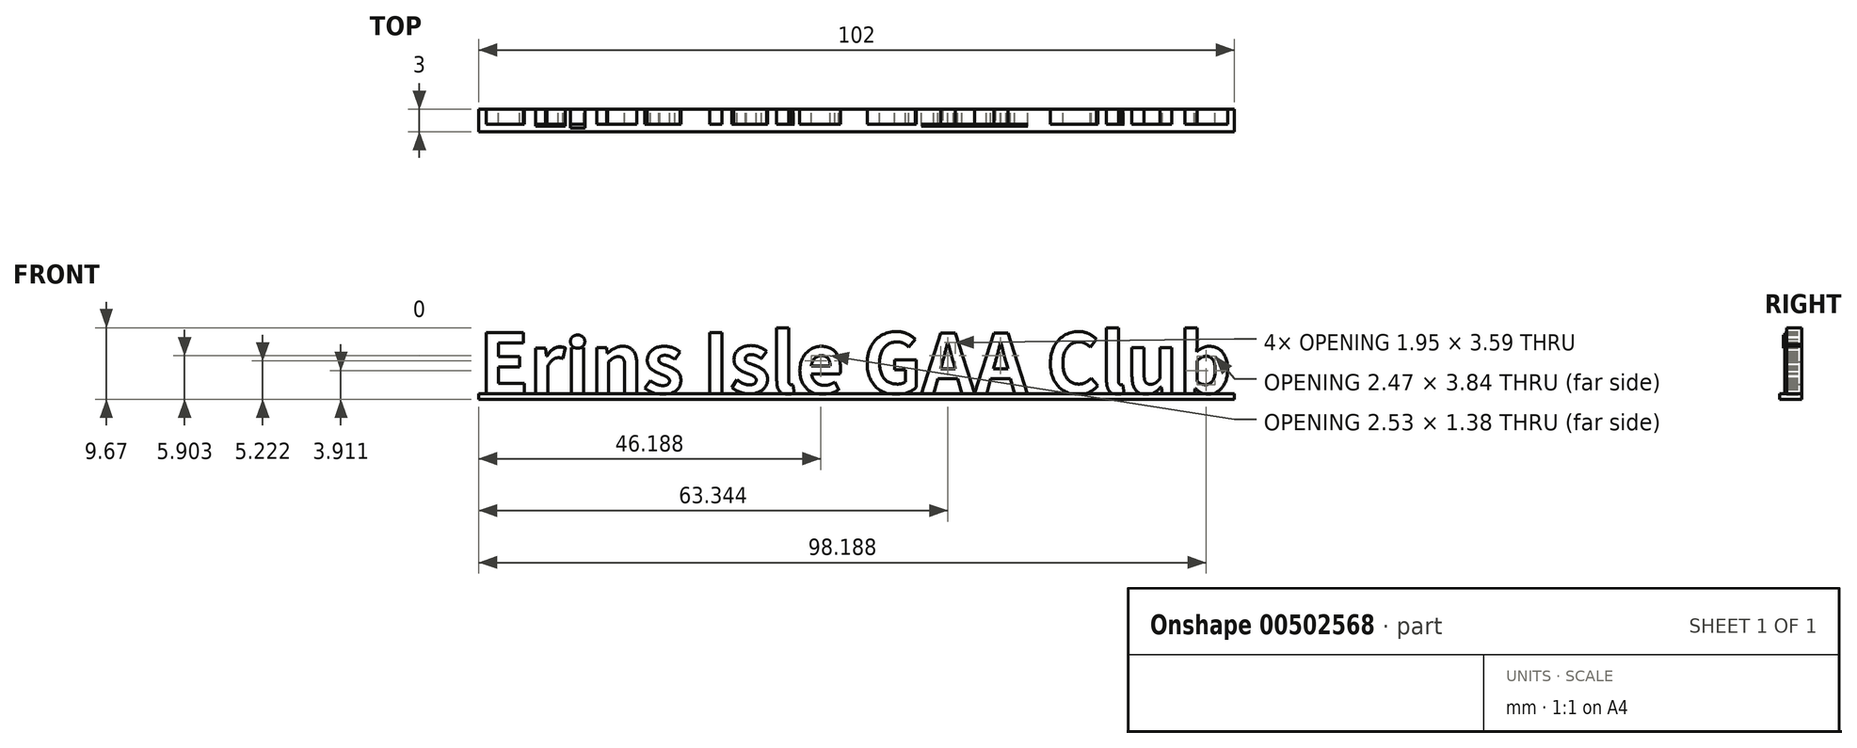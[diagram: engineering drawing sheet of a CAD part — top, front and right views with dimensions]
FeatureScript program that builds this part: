
annotation { "Feature Type Name" : "Feature", "Feature Type Description" : "" }
export const myFeature = defineFeature(function(context is Context, id is Id, definition is map)
    precondition{}
    {
        {
            var Q0;
            Q0=qCreatedBy(makeId("Front.planeOp"),FACE);
            var sketch = newSketch(context, id + "F0", { "sketchPlane" : qUnion([Q0])});
            skText(sketch, "E0", { "text": "Erins Isle GAA Club", "fontName": "NotoSansCJKjp-Bold.otf"});
            const initialGuessF0  = {"E0": [0, 0, 1, 0, 0.008]};
            skSetInitialGuess(sketch, initialGuessF0);
            skSolve(sketch);
        }
        {
            var Q0;
            Q0=qSketchRegion(id+"F0",true);
            extrude(context, id + "F1", {"entities" : qUnion([Q0]), "depth" : 2 * mm, "offsetDistance" : 25 * mm});
        }
        {
            var Q0;
            Q0=makeQuery(id+"F1.opExtrude","SWEPT_BODY",BODY,{"disambiguationData":[OSD([sQuery(id+"F0.wireOp",EDGE,"E0.sketch_text.stroke-51"),sQuery(id+"F0.wireOp",EDGE,"E0.sketch_text.stroke-52"),sQuery(id+"F0.wireOp",EDGE,"E0.sketch_text.stroke-53"),sQuery(id+"F0.wireOp",EDGE,"E0.sketch_text.stroke-54"),sQuery(id+"F0.wireOp",EDGE,"E0.sketch_text.stroke-55"),sQuery(id+"F0.wireOp",EDGE,"E0.sketch_text.stroke-56"),sQuery(id+"F0.wireOp",EDGE,"E0.sketch_text.stroke-57"),sQuery(id+"F0.wireOp",EDGE,"E0.sketch_text.stroke-58"),sQuery(id+"F0.wireOp",EDGE,"E0.sketch_text.stroke-59"),sQuery(id+"F0.wireOp",EDGE,"E0.sketch_text.stroke-60"),sQuery(id+"F0.wireOp",EDGE,"E0.sketch_text.stroke-61"),sQuery(id+"F0.wireOp",EDGE,"E0.sketch_text.stroke-62"),sQuery(id+"F0.wireOp",EDGE,"E0.sketch_text.stroke-63"),sQuery(id+"F0.wireOp",EDGE,"E0.sketch_text.stroke-64"),sQuery(id+"F0.wireOp",EDGE,"E0.sketch_text.stroke-65"),sQuery(id+"F0.wireOp",EDGE,"E0.sketch_text.stroke-66"),sQuery(id+"F0.wireOp",EDGE,"E0.sketch_text.stroke-67"),sQuery(id+"F0.wireOp",EDGE,"E0.sketch_text.stroke-68"),sQuery(id+"F0.wireOp",EDGE,"E0.sketch_text.stroke-69"),sQuery(id+"F0.wireOp",EDGE,"E0.sketch_text.stroke-70"),sQuery(id+"F0.wireOp",EDGE,"E0.sketch_text.stroke-71"),sQuery(id+"F0.wireOp",EDGE,"E0.sketch_text.stroke-72"),sQuery(id+"F0.wireOp",EDGE,"E0.sketch_text.stroke-73"),sQuery(id+"F0.wireOp",EDGE,"E0.sketch_text.stroke-74"),sQuery(id+"F0.wireOp",EDGE,"E0.sketch_text.stroke-75"),sQuery(id+"F0.wireOp",EDGE,"E0.sketch_text.stroke-76"),sQuery(id+"F0.wireOp",EDGE,"E0.sketch_text.stroke-77"),sQuery(id+"F0.wireOp",EDGE,"E0.sketch_text.stroke-78"),sQuery(id+"F0.wireOp",EDGE,"E0.sketch_text.stroke-79"),sQuery(id+"F0.wireOp",EDGE,"E0.sketch_text.stroke-80")])]});
            transform(context, id + "F2", {"entities" : qUnion([Q0]), "transformType" : TransformType.TRANSLATION_3D, "dx" : 0 * mm, "dy" : 0 * mm, "dz" : 2.4 * mm, "makeCopy" : false});
        }
        {
            var Q0;
            Q0=makeQuery(id+"F1.opExtrude","SWEPT_BODY",BODY,{"disambiguationData":[OSD([sQuery(id+"F0.wireOp",EDGE,"E0.sketch_text.stroke-109"),sQuery(id+"F0.wireOp",EDGE,"E0.sketch_text.stroke-110"),sQuery(id+"F0.wireOp",EDGE,"E0.sketch_text.stroke-111"),sQuery(id+"F0.wireOp",EDGE,"E0.sketch_text.stroke-112")])]});
            var Q1;
            Q1=makeQuery(id+"F1.opExtrude","SWEPT_BODY",BODY,{"disambiguationData":[OSD([sQuery(id+"F0.wireOp",EDGE,"E0.sketch_text.stroke-20"),sQuery(id+"F0.wireOp",EDGE,"E0.sketch_text.stroke-21"),sQuery(id+"F0.wireOp",EDGE,"E0.sketch_text.stroke-22"),sQuery(id+"F0.wireOp",EDGE,"E0.sketch_text.stroke-23")])]});
            transform(context, id + "F3", {"entities" : qUnion([Q0, Q1]), "transformType" : TransformType.TRANSLATION_3D, "dx" : 0 * mm, "dy" : 0 * mm, "dz" : -1.1 * mm, "makeCopy" : false});
        }
        {
            var Q0;
            Q0=makeQuery(id+"F1.opExtrude","CAP_FACE",FACE,{"disambiguationData":[OSD([sQuery(id+"F0.wireOp",EDGE,"E0.sketch_text.stroke-20"),sQuery(id+"F0.wireOp",EDGE,"E0.sketch_text.stroke-21"),sQuery(id+"F0.wireOp",EDGE,"E0.sketch_text.stroke-22"),sQuery(id+"F0.wireOp",EDGE,"E0.sketch_text.stroke-23")])],"isStart":false});
            var Q1;
            Q1=makeQuery(id+"F1.opExtrude","CAP_FACE",FACE,{"disambiguationData":[OSD([sQuery(id+"F0.wireOp",EDGE,"E0.sketch_text.stroke-109"),sQuery(id+"F0.wireOp",EDGE,"E0.sketch_text.stroke-110"),sQuery(id+"F0.wireOp",EDGE,"E0.sketch_text.stroke-111"),sQuery(id+"F0.wireOp",EDGE,"E0.sketch_text.stroke-112")])],"isStart":false});
            extrude(context, id + "F4", {"entities" : qUnion([Q0, Q1]), "depth" : 0.3 * mm, "offsetDistance" : 25 * mm});
        }
        {
            var Q0;
            Q0=qCreatedBy(makeId("Front.planeOp"),FACE);
            var sketch = newSketch(context, id + "F5", { "sketchPlane" : qUnion([Q0])});
            skLineSegment(sketch, "E1.bottom", {"start": v(0, 0) * mm, "end": v(102, 0) * mm});
            skLineSegment(sketch, "E1.top", {"start": v(0, -0.8) * mm, "end": v(102, -0.8) * mm});
            skLineSegment(sketch, "E1.left", {"start": v(0, 0) * mm, "end": v(0, -0.8) * mm});
            skLineSegment(sketch, "E1.right", {"start": v(102, 0) * mm, "end": v(102, -0.8) * mm});
            skSolve(sketch);
        }
        {
            var Q0;
            Q0=makeQuery(id+"F5.imprint","IMPRINT",FACE,{"disambiguationData":[TD([[makeQuery(id+"F5.imprint","IMPRINT",EDGE,{"derivedFrom":sQuery(id+"F5.wireOp",EDGE,"E1.bottom")}),-1.0]])]});
            extrude(context, id + "F6", {"entities" : qUnion([Q0]), "depth" : 3 * mm, "offsetDistance" : 25 * mm});
        }
        {
            var Q0;
            Q0=makeQuery(id+"F1.opExtrude","SWEPT_BODY",BODY,{"disambiguationData":[OSD([sQuery(id+"F0.wireOp",EDGE,"E0.sketch_text.stroke-62"),sQuery(id+"F0.wireOp",EDGE,"E0.sketch_text.stroke-63"),sQuery(id+"F0.wireOp",EDGE,"E0.sketch_text.stroke-64"),sQuery(id+"F0.wireOp",EDGE,"E0.sketch_text.stroke-65"),sQuery(id+"F0.wireOp",EDGE,"E0.sketch_text.stroke-66"),sQuery(id+"F0.wireOp",EDGE,"E0.sketch_text.stroke-67"),sQuery(id+"F0.wireOp",EDGE,"E0.sketch_text.stroke-68"),sQuery(id+"F0.wireOp",EDGE,"E0.sketch_text.stroke-69"),sQuery(id+"F0.wireOp",EDGE,"E0.sketch_text.stroke-70"),sQuery(id+"F0.wireOp",EDGE,"E0.sketch_text.stroke-71"),sQuery(id+"F0.wireOp",EDGE,"E0.sketch_text.stroke-72"),sQuery(id+"F0.wireOp",EDGE,"E0.sketch_text.stroke-73"),sQuery(id+"F0.wireOp",EDGE,"E0.sketch_text.stroke-74"),sQuery(id+"F0.wireOp",EDGE,"E0.sketch_text.stroke-75")])]});
            transform(context, id + "F7", {"entities" : qUnion([Q0]), "transformType" : TransformType.TRANSLATION_3D, "dx" : 0 * mm, "dy" : 0 * mm, "dz" : -2.3 * mm, "makeCopy" : false});
        }
        {
            var Q0;
            Q0=makeQuery(id+"F4.opExtrude","SWEPT_BODY",BODY,{"disambiguationData":[OSD([sQuery(id+"F0.wireOp",EDGE,"E0.sketch_text.stroke-12"),sQuery(id+"F0.wireOp",EDGE,"E0.sketch_text.stroke-13"),sQuery(id+"F0.wireOp",EDGE,"E0.sketch_text.stroke-14"),sQuery(id+"F0.wireOp",EDGE,"E0.sketch_text.stroke-15"),sQuery(id+"F0.wireOp",EDGE,"E0.sketch_text.stroke-16"),sQuery(id+"F0.wireOp",EDGE,"E0.sketch_text.stroke-17"),sQuery(id+"F0.wireOp",EDGE,"E0.sketch_text.stroke-18"),sQuery(id+"F0.wireOp",EDGE,"E0.sketch_text.stroke-19"),sQuery(id+"F0.wireOp",EDGE,"E0.sketch_text.stroke-20"),sQuery(id+"F0.wireOp",EDGE,"E0.sketch_text.stroke-21"),sQuery(id+"F0.wireOp",EDGE,"E0.sketch_text.stroke-22")])]});
            transform(context, id + "F8", {"entities" : qUnion([Q0]), "transformType" : TransformType.TRANSLATION_3D, "dx" : 0 * mm, "dy" : 0 * mm, "dz" : 1 * mm, "makeCopy" : false});
        }
        {
            var Q0;
            Q0=makeQuery(id+"F1.opExtrude","SWEPT_BODY",BODY,{"disambiguationData":[OSD([sQuery(id+"F0.wireOp",EDGE,"E0.sketch_text.stroke-12"),sQuery(id+"F0.wireOp",EDGE,"E0.sketch_text.stroke-13"),sQuery(id+"F0.wireOp",EDGE,"E0.sketch_text.stroke-14"),sQuery(id+"F0.wireOp",EDGE,"E0.sketch_text.stroke-15"),sQuery(id+"F0.wireOp",EDGE,"E0.sketch_text.stroke-16"),sQuery(id+"F0.wireOp",EDGE,"E0.sketch_text.stroke-17"),sQuery(id+"F0.wireOp",EDGE,"E0.sketch_text.stroke-18"),sQuery(id+"F0.wireOp",EDGE,"E0.sketch_text.stroke-19"),sQuery(id+"F0.wireOp",EDGE,"E0.sketch_text.stroke-20"),sQuery(id+"F0.wireOp",EDGE,"E0.sketch_text.stroke-21"),sQuery(id+"F0.wireOp",EDGE,"E0.sketch_text.stroke-22")])]});
            var Q1;
            Q1=makeQuery(id+"F4.opExtrude","SWEPT_BODY",BODY,{"disambiguationData":[OSD([sQuery(id+"F0.wireOp",EDGE,"E0.sketch_text.stroke-110"),sQuery(id+"F0.wireOp",EDGE,"E0.sketch_text.stroke-111"),sQuery(id+"F0.wireOp",EDGE,"E0.sketch_text.stroke-112"),sQuery(id+"F0.wireOp",EDGE,"E0.sketch_text.stroke-113"),sQuery(id+"F0.wireOp",EDGE,"E0.sketch_text.stroke-114"),sQuery(id+"F0.wireOp",EDGE,"E0.sketch_text.stroke-115"),sQuery(id+"F0.wireOp",EDGE,"E0.sketch_text.stroke-116"),sQuery(id+"F0.wireOp",EDGE,"E0.sketch_text.stroke-117"),sQuery(id+"F0.wireOp",EDGE,"E0.sketch_text.stroke-118"),sQuery(id+"F0.wireOp",EDGE,"E0.sketch_text.stroke-119"),sQuery(id+"F0.wireOp",EDGE,"E0.sketch_text.stroke-120"),sQuery(id+"F0.wireOp",EDGE,"E0.sketch_text.stroke-121"),sQuery(id+"F0.wireOp",EDGE,"E0.sketch_text.stroke-122"),sQuery(id+"F0.wireOp",EDGE,"E0.sketch_text.stroke-123"),sQuery(id+"F0.wireOp",EDGE,"E0.sketch_text.stroke-124"),sQuery(id+"F0.wireOp",EDGE,"E0.sketch_text.stroke-125"),sQuery(id+"F0.wireOp",EDGE,"E0.sketch_text.stroke-126"),sQuery(id+"F0.wireOp",EDGE,"E0.sketch_text.stroke-127"),sQuery(id+"F0.wireOp",EDGE,"E0.sketch_text.stroke-128"),sQuery(id+"F0.wireOp",EDGE,"E0.sketch_text.stroke-129"),sQuery(id+"F0.wireOp",EDGE,"E0.sketch_text.stroke-130"),sQuery(id+"F0.wireOp",EDGE,"E0.sketch_text.stroke-131"),sQuery(id+"F0.wireOp",EDGE,"E0.sketch_text.stroke-132"),sQuery(id+"F0.wireOp",EDGE,"E0.sketch_text.stroke-133"),sQuery(id+"F0.wireOp",EDGE,"E0.sketch_text.stroke-134"),sQuery(id+"F0.wireOp",EDGE,"E0.sketch_text.stroke-135"),sQuery(id+"F0.wireOp",EDGE,"E0.sketch_text.stroke-136"),sQuery(id+"F0.wireOp",EDGE,"E0.sketch_text.stroke-137")])]});
            var Q2;
            Q2=makeQuery(id+"F1.opExtrude","SWEPT_BODY",BODY,{"disambiguationData":[OSD([sQuery(id+"F0.wireOp",EDGE,"E0.sketch_text.stroke-110"),sQuery(id+"F0.wireOp",EDGE,"E0.sketch_text.stroke-111"),sQuery(id+"F0.wireOp",EDGE,"E0.sketch_text.stroke-112"),sQuery(id+"F0.wireOp",EDGE,"E0.sketch_text.stroke-113"),sQuery(id+"F0.wireOp",EDGE,"E0.sketch_text.stroke-114"),sQuery(id+"F0.wireOp",EDGE,"E0.sketch_text.stroke-115"),sQuery(id+"F0.wireOp",EDGE,"E0.sketch_text.stroke-116"),sQuery(id+"F0.wireOp",EDGE,"E0.sketch_text.stroke-117"),sQuery(id+"F0.wireOp",EDGE,"E0.sketch_text.stroke-118"),sQuery(id+"F0.wireOp",EDGE,"E0.sketch_text.stroke-119"),sQuery(id+"F0.wireOp",EDGE,"E0.sketch_text.stroke-120"),sQuery(id+"F0.wireOp",EDGE,"E0.sketch_text.stroke-121"),sQuery(id+"F0.wireOp",EDGE,"E0.sketch_text.stroke-122"),sQuery(id+"F0.wireOp",EDGE,"E0.sketch_text.stroke-123"),sQuery(id+"F0.wireOp",EDGE,"E0.sketch_text.stroke-124"),sQuery(id+"F0.wireOp",EDGE,"E0.sketch_text.stroke-125"),sQuery(id+"F0.wireOp",EDGE,"E0.sketch_text.stroke-126"),sQuery(id+"F0.wireOp",EDGE,"E0.sketch_text.stroke-127"),sQuery(id+"F0.wireOp",EDGE,"E0.sketch_text.stroke-128"),sQuery(id+"F0.wireOp",EDGE,"E0.sketch_text.stroke-129"),sQuery(id+"F0.wireOp",EDGE,"E0.sketch_text.stroke-130"),sQuery(id+"F0.wireOp",EDGE,"E0.sketch_text.stroke-131"),sQuery(id+"F0.wireOp",EDGE,"E0.sketch_text.stroke-132"),sQuery(id+"F0.wireOp",EDGE,"E0.sketch_text.stroke-133"),sQuery(id+"F0.wireOp",EDGE,"E0.sketch_text.stroke-134"),sQuery(id+"F0.wireOp",EDGE,"E0.sketch_text.stroke-135"),sQuery(id+"F0.wireOp",EDGE,"E0.sketch_text.stroke-136"),sQuery(id+"F0.wireOp",EDGE,"E0.sketch_text.stroke-137")])]});
            transform(context, id + "F9", {"entities" : qUnion([Q0, Q1, Q2]), "transformType" : TransformType.TRANSLATION_3D, "dx" : 0 * mm, "dy" : 0 * mm, "dz" : 1.02 * mm, "makeCopy" : false});
        }
        {
            var Q0;
            Q0=makeQuery(id+"F1.opExtrude","SWEPT_BODY",BODY,{"disambiguationData":[OSD([sQuery(id+"F0.wireOp",EDGE,"E0.sketch_text.stroke-27"),sQuery(id+"F0.wireOp",EDGE,"E0.sketch_text.stroke-28"),sQuery(id+"F0.wireOp",EDGE,"E0.sketch_text.stroke-29"),sQuery(id+"F0.wireOp",EDGE,"E0.sketch_text.stroke-30")])]});
            transform(context, id + "F10", {"entities" : qUnion([Q0]), "transformType" : TransformType.TRANSLATION_3D, "dx" : 0 * mm, "dy" : 0 * mm, "dz" : -1.1 * mm, "makeCopy" : false});
        }
        {
            var Q0;
            Q0=makeQuery(id+"F1.opExtrude","CAP_FACE",FACE,{"disambiguationData":[OSD([sQuery(id+"F0.wireOp",EDGE,"E0.sketch_text.stroke-27"),sQuery(id+"F0.wireOp",EDGE,"E0.sketch_text.stroke-28"),sQuery(id+"F0.wireOp",EDGE,"E0.sketch_text.stroke-29"),sQuery(id+"F0.wireOp",EDGE,"E0.sketch_text.stroke-30")])],"isStart":false});
            extrude(context, id + "F11", {"entities" : qUnion([Q0]), "depth" : .5 * mm, "offsetDistance" : 25 * mm});
        }
    });
